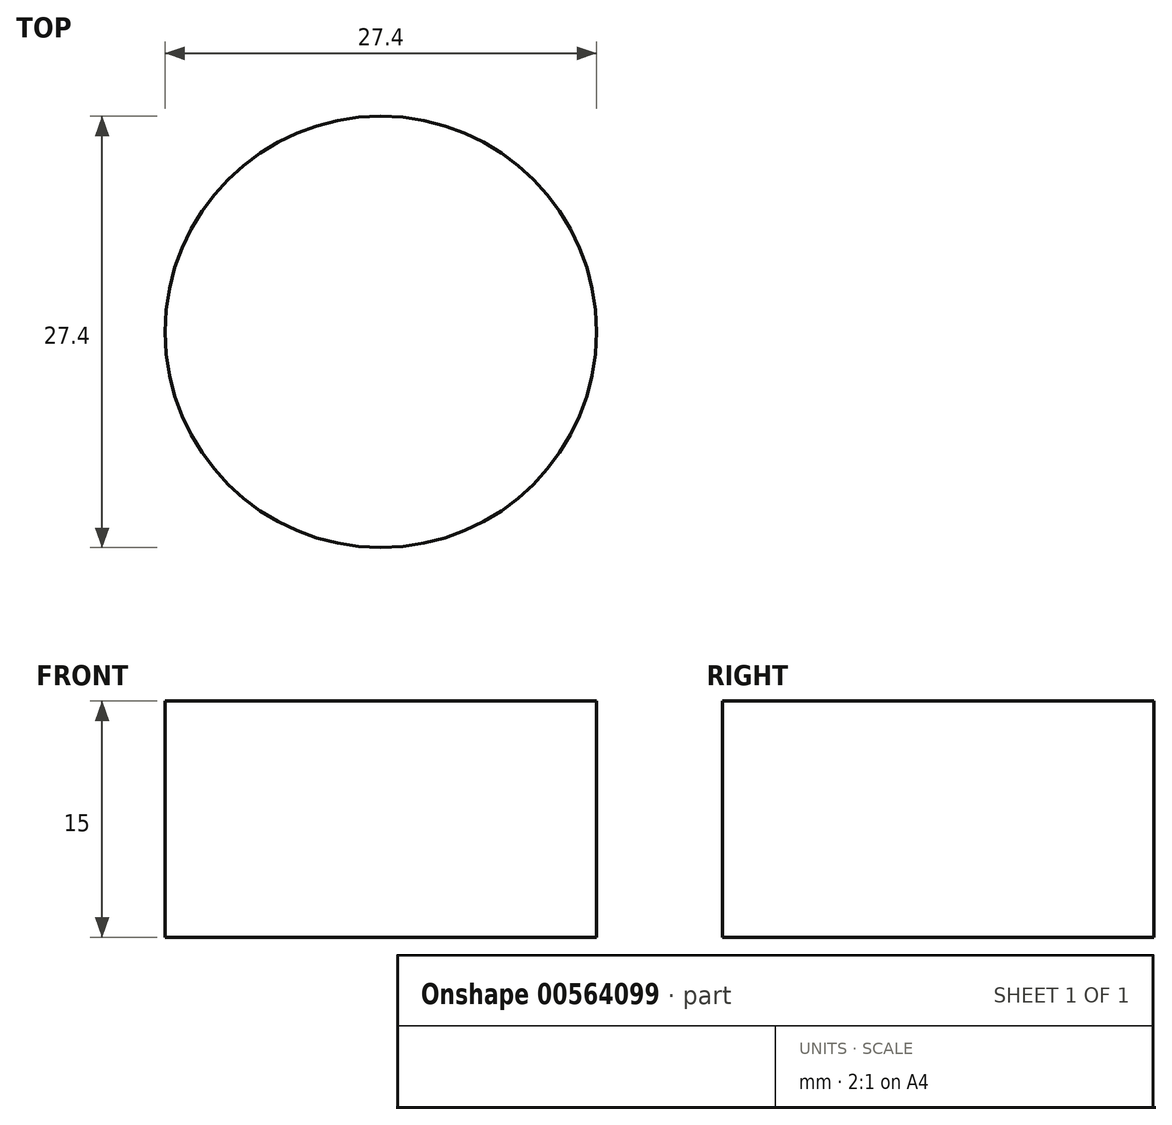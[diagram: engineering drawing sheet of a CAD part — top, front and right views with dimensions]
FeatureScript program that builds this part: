
annotation { "Feature Type Name" : "Feature", "Feature Type Description" : "" }
export const myFeature = defineFeature(function(context is Context, id is Id, definition is map)
    precondition{}
    {
        {
            var Q0;
            Q0=qCreatedBy(makeId("Top.planeOp"),FACE);
            var sketch = newSketch(context, id + "F0", { "sketchPlane" : qUnion([Q0])});
            skCircle(sketch, "E0", {"center": v(0, 0) * mm, "radius": 12.7 * mm});
            skCircle(sketch, "E1.0", {"center": v(0, 0) * mm, "radius": 13.7 * mm});
            skSolve(sketch);
        }
        {
            var Q0;
            Q0=makeQuery(id+"F0.imprint","IMPRINT",FACE,{"disambiguationData":[TD([[makeQuery(id+"F0.imprint","IMPRINT",EDGE,{"derivedFrom":sQuery(id+"F0.wireOp",EDGE,"E0")}),-1.0]])]});
            var Q1;
            Q1=makeQuery(id+"F0.imprint","IMPRINT",FACE,{"disambiguationData":[TD([[makeQuery(id+"F0.imprint","IMPRINT",EDGE,{"derivedFrom":sQuery(id+"F0.wireOp",EDGE,"E0")}),1.0]])]});
            extrude(context, id + "F1", {"entities" : qUnion([Q0, Q1]), "depth" : 15 * mm, "offsetDistance" : 25 * mm});
        }
    });
